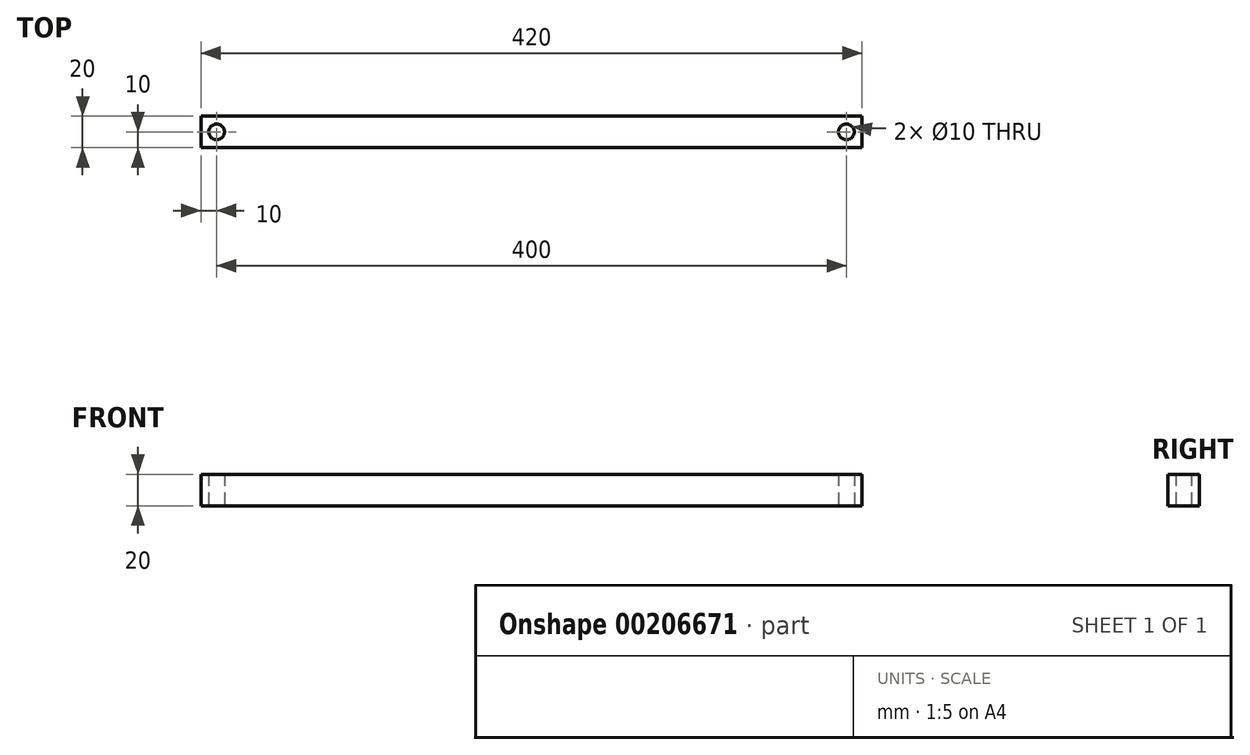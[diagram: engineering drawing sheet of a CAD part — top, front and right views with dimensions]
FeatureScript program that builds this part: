
annotation { "Feature Type Name" : "Feature", "Feature Type Description" : "" }
export const myFeature = defineFeature(function(context is Context, id is Id, definition is map)
    precondition{}
    {
        {
            var Q0;
            Q0=qCreatedBy(makeId("Top.planeOp"),FACE);
            var sketch = newSketch(context, id + "F0", { "sketchPlane" : qUnion([Q0])});
            skCircle(sketch, "E0", {"center": v(0, 0) * mm, "radius": 5 * mm});
            skCircle(sketch, "E1", {"center": v(400, 0) * mm, "radius": 5 * mm});
            skLineSegment(sketch, "E2.bottom", {"start": v(-10, 10) * mm, "end": v(410, 10) * mm});
            skLineSegment(sketch, "E2.top", {"start": v(-10, -10) * mm, "end": v(410, -10) * mm});
            skLineSegment(sketch, "E2.left", {"start": v(-10, 10) * mm, "end": v(-10, -10) * mm});
            skLineSegment(sketch, "E2.right", {"start": v(410, 10) * mm, "end": v(410, -10) * mm});
            skSolve(sketch);
        }
        {
            var Q0;
            Q0=makeQuery(id+"F0.imprint","IMPRINT",FACE,{"disambiguationData":[TD([[makeQuery(id+"F0.imprint","IMPRINT",EDGE,{"derivedFrom":sQuery(id+"F0.wireOp",EDGE,"E0")}),-1.0]])]});
            extrude(context, id + "F1", {"entities" : qUnion([Q0]), "depth" : 20 * mm});
        }
    });
